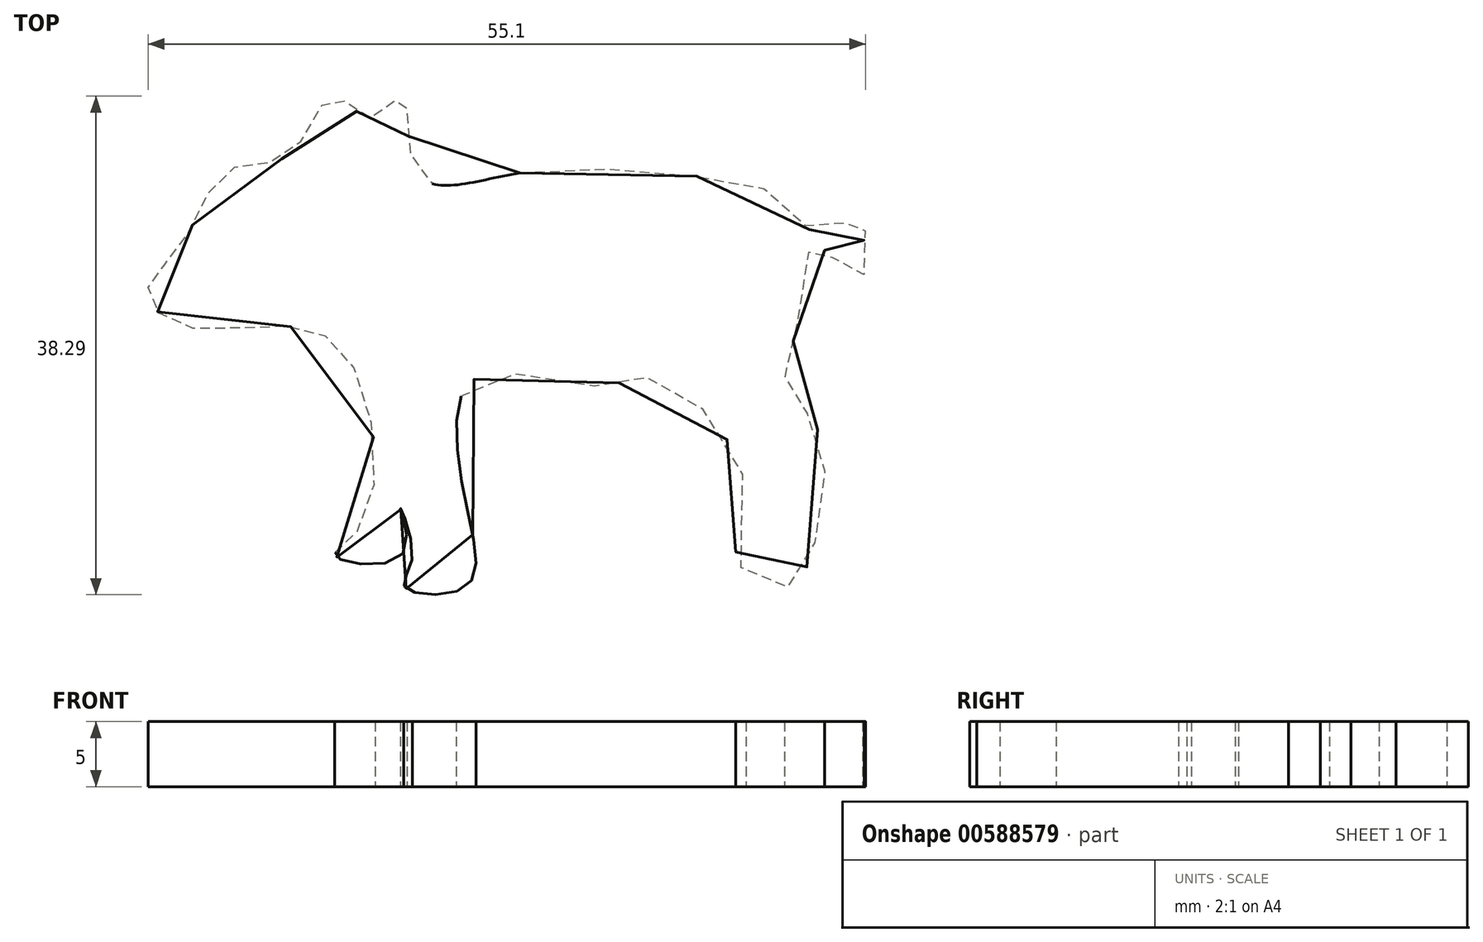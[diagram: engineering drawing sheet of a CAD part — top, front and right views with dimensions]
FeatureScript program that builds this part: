
annotation { "Feature Type Name" : "Feature", "Feature Type Description" : "" }
export const myFeature = defineFeature(function(context is Context, id is Id, definition is map)
    precondition{}
    {
        {
            var Q0;
            Q0=qCreatedBy(makeId("Top.planeOp"),FACE);
            var sketch = newSketch(context, id + "F0", { "sketchPlane" : qUnion([Q0])});
            skFitSpline(sketch, "E0", {"points": [v(-5.8, 41.3) * mm, v(6.9, 41.12) * mm, v(14.63, 39.1) * mm, v(17.39, 36.52) * mm, v(20.52, 38.18) * mm, v(20.52, 34.87) * mm, v(20.52, 33.4) * mm, v(18.12, 34.87) * mm, v(16.65, 35.79) * mm, v(15.36, 29.16) * mm, v(14.63, 24.93) * mm, v(17.02, 21.62) * mm, v(17.02, 13.7) * mm, v(14.63, 9.48) * mm, v(10.95, 11.32) * mm, v(11.13, 13.52) * mm, v(10.95, 19.23) * mm, v(4.7, 25.48) * mm, v(0, 24.93) * mm, v(-9.3, 25.48) * mm, v(-10.03, 16.28) * mm, v(-10.03, 9.48) * mm, v(-14.63, 9.48) * mm, v(-14.08, 11.87) * mm, v(-15, 15.55) * mm, v(-14.81, 12.05) * mm, v(-19.96, 11.87) * mm, v(-17.94, 14.26) * mm, v(-18.68, 26.59) * mm, v(-24.01, 29.53) * mm, v(-32.3, 29.72) * mm, v(-34.35, 32.48) * mm, v(-31.92, 35.6) * mm, v(-28.24, 41.5) * mm, v(-23.46, 42.78) * mm, v(-20.15, 47.2) * mm, v(-17.2, 45.54) * mm, v(-14.81, 47.2) * mm, v(-13.7, 41.3) * mm, v(-5.8, 41.3) * mm]});
            skSolve(sketch);
        }
        {
            var Q0;
            Q0 = qSketchRegion(id + "F0", true);
            extrude(context, id + "F1", {"entities" : qUnion([Q0]), "depth" : 5 * mm, "offsetDistance" : 25 * mm});
        }
    });
